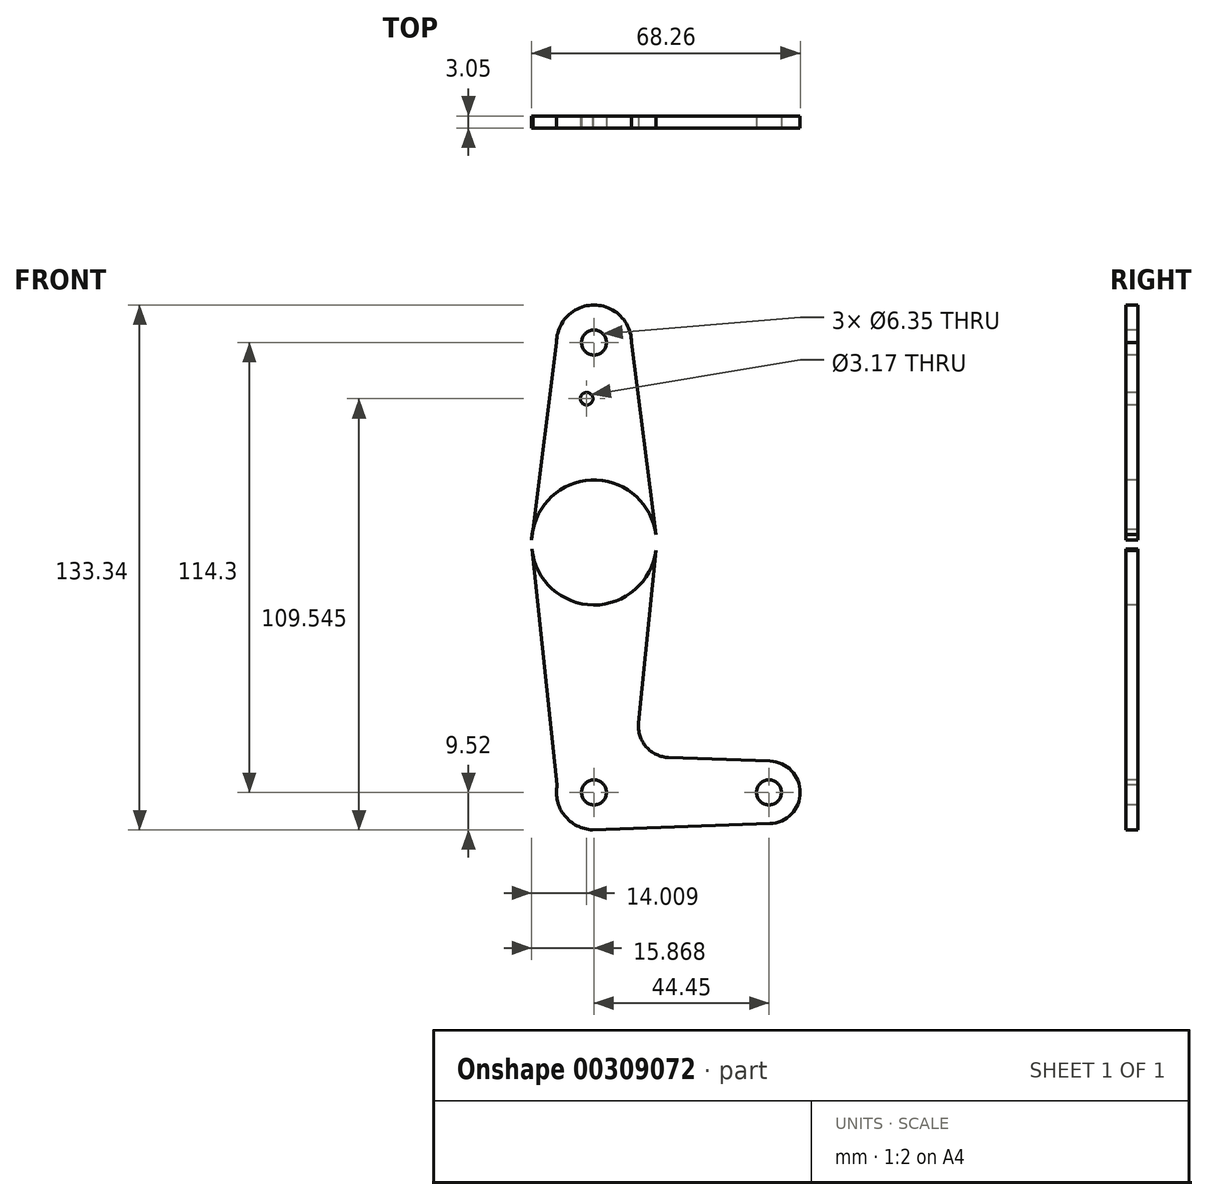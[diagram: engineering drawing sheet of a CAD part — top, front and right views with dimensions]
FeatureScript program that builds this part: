
annotation { "Feature Type Name" : "Feature", "Feature Type Description" : "" }
export const myFeature = defineFeature(function(context is Context, id is Id, definition is map)
    precondition{}
    {
        {
            var Q0;
            Q0=qCreatedBy(makeId("Front.planeOp"),FACE);
            var sketch = newSketch(context, id + "F0", { "sketchPlane" : qUnion([Q0])});
            skLineSegment(sketch, "E0", {"start": v(-45.86, 64.07) * mm, "end": v(-45.86, -50.23) * mm});
            skLineSegment(sketch, "E1", {"start": v(-45.86, -50.23) * mm, "end": v(-1.41, -50.23) * mm});
            skCircle(sketch, "E2", {"center": v(-45.86, 64.07) * mm, "radius": 9.53 * mm});
            skCircle(sketch, "E3", {"center": v(-45.86, 13.27) * mm, "radius": 15.88 * mm});
            skCircle(sketch, "E4", {"center": v(-45.86, -50.23) * mm, "radius": 9.53 * mm});
            skCircle(sketch, "E5", {"center": v(-1.41, -50.23) * mm, "radius": 7.94 * mm});
            skLineSegment(sketch, "E6", {"start": v(-36.34, 64.07) * mm, "end": v(-30.11, 15.28) * mm});
            skLineSegment(sketch, "E7", {"start": v(-55.39, 64.04) * mm, "end": v(-61.73, 13.88) * mm});
            skLineSegment(sketch, "E8", {"start": v(-61.65, 11.57) * mm, "end": v(-55.2, -48.38) * mm});
            skLineSegment(sketch, "E9", {"start": v(-30.11, 11.26) * mm, "end": v(-34.52, -32.64) * mm});
            skLineSegment(sketch, "E10", {"start": v(-26.9, -41.38) * mm, "end": v(0, -42.34) * mm});
            skLineSegment(sketch, "E11", {"start": v(-46.25, -59.75) * mm, "end": v(0, -58.12) * mm});
            skCircle(sketch, "E12", {"center": v(-45.86, 64.07) * mm, "radius": 3.18 * mm});
            skCircle(sketch, "E13", {"center": v(-45.86, 13.27) * mm, "radius": 3.18 * mm});
            skCircle(sketch, "E14", {"center": v(-45.86, -50.23) * mm, "radius": 3.18 * mm});
            skCircle(sketch, "E15", {"center": v(-1.41, -50.23) * mm, "radius": 3.18 * mm});
            skCircle(sketch, "E16", {"center": v(-47.72, 49.8) * mm, "radius": 1.59 * mm});
            skArc(sketch, "E17.filletArc", {"start": v(-34.52, -32.64) * mm, "mid": v(-32.6, -38.66) * mm, "end": v(-26.9, -41.38) * mm});
            skSolve(sketch);
        }
        {
            var Q0;
            {var subQ0=sQuery(id+"F0.wireOp",EDGE,"E7");var subQ1=sQuery(id+"F0.wireOp",EDGE,"E3");var subQ2=makeQuery(id+"F0.imprint","INTERSECT",VERTEX,{"disambiguationData":[OD(0.0)],"derivedFrom":[subQ1,subQ0]});Q0=makeQuery(id+"F0.imprint","IMPRINT",FACE,{"disambiguationData":[TD([[makeQuery(id+"F0.imprint","IMPRINT",EDGE,{"disambiguationData":[TD([[subQ2,1.0]])],"derivedFrom":subQ1}),1.0]])]});}
            var Q1;
            {var subQ0=sQuery(id+"F0.wireOp",EDGE,"E11");var subQ1=sQuery(id+"F0.wireOp",EDGE,"E4");var subQ2=makeQuery(id+"F0.imprint","INTERSECT",VERTEX,{"disambiguationData":[OD(0.0)],"derivedFrom":[subQ1,subQ0]});Q1=makeQuery(id+"F0.imprint","IMPRINT",FACE,{"disambiguationData":[TD([[makeQuery(id+"F0.imprint","IMPRINT",EDGE,{"disambiguationData":[TD([[subQ2,-1.0]])],"derivedFrom":subQ1}),1.0]])]});}
            var Q2;
            {var subQ5=sQuery(id+"F0.wireOp",EDGE,"E8");Q2=makeQuery(id+"F0.imprint","IMPRINT",FACE,{"disambiguationData":[TD([[makeQuery(id+"F0.imprint","IMPRINT",EDGE,{"derivedFrom":subQ5}),1.0]])]});}
            var Q3;
            {var subQ0=sQuery(id+"F0.wireOp",EDGE,"E5");var subQ1=sQuery(id+"F0.wireOp",EDGE,"E1");var subQ2=makeQuery(id+"F0.imprint","INTERSECT",VERTEX,{"derivedFrom":[subQ1,subQ0]});Q3=makeQuery(id+"F0.imprint","IMPRINT",FACE,{"disambiguationData":[TD([[makeQuery(id+"F0.imprint","IMPRINT",EDGE,{"disambiguationData":[TD([[subQ2,1.0]])],"derivedFrom":subQ1}),-1.0]])]});}
            var Q4;
            Q4=makeQuery(id+"F0.imprint","IMPRINT",FACE,{"disambiguationData":[TD([[makeQuery(id+"F0.imprint","IMPRINT",EDGE,{"derivedFrom":sQuery(id+"F0.wireOp",EDGE,"E12")}),-1.0]])]});
            var Q5;
            Q5=makeQuery(id+"F0.imprint","IMPRINT",FACE,{"disambiguationData":[TD([[makeQuery(id+"F0.imprint","IMPRINT",EDGE,{"derivedFrom":sQuery(id+"F0.wireOp",EDGE,"E15")}),-1.0]])]});
            var Q6;
            {var subQ0=sQuery(id+"F0.wireOp",EDGE,"E3");var subQ2=sQuery(id+"F0.wireOp",EDGE,"E0");var subQ5=makeQuery(id+"F0.imprint","INTERSECT",VERTEX,{"disambiguationData":[OD(0.0)],"derivedFrom":[subQ2,subQ0]});Q6=makeQuery(id+"F0.imprint","IMPRINT",FACE,{"disambiguationData":[TD([[makeQuery(id+"F0.imprint","IMPRINT",EDGE,{"disambiguationData":[TD([[subQ5,-1.0]])],"derivedFrom":subQ2}),1.0]])]});}
            var Q7;
            {var subQ1=sQuery(id+"F0.wireOp",EDGE,"E3");var subQ3=sQuery(id+"F0.wireOp",EDGE,"E0");var subQ4=makeQuery(id+"F0.imprint","INTERSECT",VERTEX,{"disambiguationData":[OD(0.0)],"derivedFrom":[subQ3,subQ1]});Q7=makeQuery(id+"F0.imprint","IMPRINT",FACE,{"disambiguationData":[TD([[makeQuery(id+"F0.imprint","IMPRINT",EDGE,{"disambiguationData":[TD([[subQ4,-1.0]])],"derivedFrom":subQ3}),-1.0]])]});}
            var Q8;
            {var subQ7=sQuery(id+"F0.wireOp",EDGE,"E9");Q8=makeQuery(id+"F0.imprint","IMPRINT",FACE,{"disambiguationData":[TD([[makeQuery(id+"F0.imprint","IMPRINT",EDGE,{"derivedFrom":subQ7}),-1.0]])]});}
            var Q9;
            {var subQ0=sQuery(id+"F0.wireOp",EDGE,"E4");var subQ4=sQuery(id+"F0.wireOp",EDGE,"E0");var subQ5=makeQuery(id+"F0.imprint","INTERSECT",VERTEX,{"derivedFrom":[subQ4,subQ0]});Q9=makeQuery(id+"F0.imprint","IMPRINT",FACE,{"disambiguationData":[TD([[makeQuery(id+"F0.imprint","IMPRINT",EDGE,{"disambiguationData":[TD([[subQ5,-1.0]])],"derivedFrom":subQ4}),-1.0]])]});}
            var Q10;
            Q10=makeQuery(id+"F0.imprint","IMPRINT",FACE,{"disambiguationData":[TD([[makeQuery(id+"F0.imprint","IMPRINT",EDGE,{"derivedFrom":sQuery(id+"F0.wireOp",EDGE,"E16")}),-1.0]])]});
            var Q11;
            {var subQ5=sQuery(id+"F0.wireOp",EDGE,"E6");Q11=makeQuery(id+"F0.imprint","IMPRINT",FACE,{"disambiguationData":[TD([[makeQuery(id+"F0.imprint","IMPRINT",EDGE,{"derivedFrom":subQ5}),-1.0]])]});}
            var Q12;
            {var subQ0=sQuery(id+"F0.wireOp",EDGE,"E4");var subQ1=sQuery(id+"F0.wireOp",EDGE,"E0");var subQ2=makeQuery(id+"F0.imprint","INTERSECT",VERTEX,{"derivedFrom":[subQ1,subQ0]});Q12=makeQuery(id+"F0.imprint","IMPRINT",FACE,{"disambiguationData":[TD([[makeQuery(id+"F0.imprint","IMPRINT",EDGE,{"disambiguationData":[TD([[subQ2,-1.0]])],"derivedFrom":subQ1}),1.0]])]});}
            extrude(context, id + "F1", {"entities" : qUnion([Q0, Q1, Q2, Q3, Q4, Q5, Q6, Q7, Q8, Q9, Q10, Q11, Q12]), "oppositeDirection" : true, "depth" : 3.05 * mm});
        }
    });
